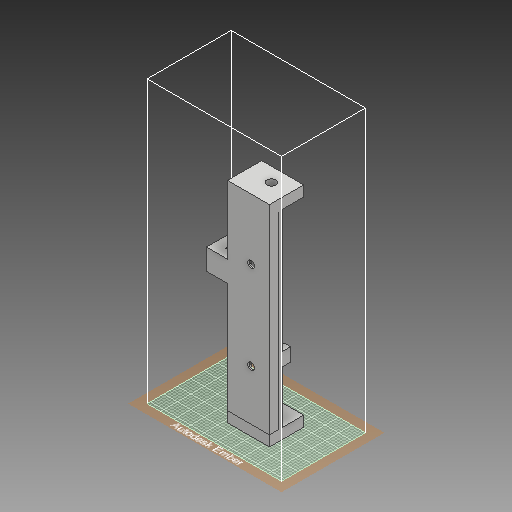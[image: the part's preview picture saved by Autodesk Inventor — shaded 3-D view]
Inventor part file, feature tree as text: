
AUTODESK INVENTOR PART (.ipt)
format: ipt  version: 2018 (Build 220112000, 112)  size: 651,776 bytes
history: native  units: mm
features: sketch x44, extrude x31, hole x8, fillet x6
ambient origin geometry x8: Origin, YZ Plane, XZ Plane, XY Plane, X Axis, Y Axis, Z Axis, Center Point
bodies: Solid1 (feature_tree)
feature tree (89):
  extrude  "Extrusion1"  Depth=100.0mm
  extrude  "Extrusion2"  Depth=5.0mm
  sketch  "Sketch3"  dims[d5=5.0mm d6=40.0mm d7=0.0mm]
  hole  "Hole1"  [1 undecoded]
  extrude  "Extrusion3"  Depth=2.0mm
  hole  "Hole2"  [1 undecoded]
  fillet  "Fillet1"  Radius=8.5mm
  extrude  "Extrusion4"  TaperAngle=90.0deg  [1 undecoded]
  extrude  "Extrusion5"  TaperAngle=180.0deg  [1 undecoded]
  hole  "Hole3"  [1 undecoded]
  fillet  "Fillet2"  Radius=3.5mm
  extrude  "Extrusion6"  Depth=10.0mm
  extrude  "Extrusion7"  Depth=5.0mm TaperAngle=0.0deg
  extrude  "Extrusion8"  Depth=5.0mm TaperAngle=0.0deg
  extrude  "Extrusion9"  Depth=0.1mm
  hole  "Hole4"  [1 undecoded]
  extrude  "Extrusion10"  Depth=5.5mm
  hole  "Hole5"  [1 undecoded]
  extrude  "Extrusion11"  Depth=2.1mm TaperAngle=0.0deg
  extrude  "Extrusion12"  Depth=5.0mm
  extrude  "Extrusion13"  Depth=1.0mm TaperAngle=0.0deg
  extrude  "Extrusion14"  Depth=3.8mm TaperAngle=0.0deg
  sketch  "Sketch21"  dims[d66=6.35mm d67=3.8mm d68=0.0mm]
  extrude  "Extrusion15"  Depth=8.0mm TaperAngle=0.0deg
  sketch  "Sketch23"  dims[d78=3.3mm d79=6.0mm d80=4.0mm d81=2.0mm d82=90.0deg d83=80.0mm d84=20.594885mm d85=5.45mm]
  extrude  "Extrusion16"  Depth=2.0mm
  extrude  "Extrusion17"  Depth=10.5mm
  hole  "Hole6"  [1 undecoded]
  fillet  "Fillet3"  Radius=4.5mm
  extrude  "Extrusion18"  Depth=8.0mm TaperAngle=0.0deg
  sketch  "Sketch28"  dims[d100=4.1mm d101=0.0mm d102=5.0mm]
  extrude  "Extrusion19"  Depth=10.0mm
  extrude  "Extrusion20"  Depth=5.0mm
  extrude  "Extrusion21"  Depth=10.0mm TaperAngle=0.0deg
  hole  "Hole7"  [1 undecoded]
  extrude  "Extrusion22"  Depth=21.0mm
  extrude  "Extrusion23"  Depth=7.499983mm TaperAngle=0.0deg
  fillet  "Fillet4"  Radius=50.0mm
  fillet  "Fillet5"  Radius=7.499983mm
  extrude  "Extrusion24"  Depth=10.0mm
  extrude  "Extrusion25"  Depth=4.1mm TaperAngle=0.0deg
  hole  "Hole8"  [1 undecoded]
  extrude  "Extrusion26"  Depth=8.0mm TaperAngle=0.0deg
  sketch  "Sketch39"  dims[d142=3.85mm d143=0.0mm d144=3.0mm]
  extrude  "Extrusion27"  Depth=1.0mm
  extrude  "Extrusion28"  Depth=3.0mm
  extrude  "Extrusion29"  Depth=100.0mm TaperAngle=0.0deg
  extrude  "Extrusion30"  Depth=10.0mm
  extrude  "Extrusion31"  Depth=7.5mm
  fillet  "Fillet6"  Radius=7.5mm
  sketch  "Sketch1"  dims[d0=22.65mm d1=100.0mm]
  sketch  "Sketch2"  dims[d2=5.0mm d3=0.0mm d4=5.0mm]
  sketch  "Sketch4"  dims[d8=10.0mm]
  sketch  "Sketch5"  dims[d9=4.0mm d10=6.0mm d11=4.0mm d12=2.0mm d13=90.0deg d14=115.0mm d15=20.594885mm d16=23.0mm]
  sketch  "Sketch6"  dims[d17=102.75mm d18=0.0mm d19=1.175mm d20=8.5mm]
  sketch  "Sketch7"  dims[d21=21.0mm d22=90.0deg]
  sketch  "Sketch8"  dims[d23=8.5mm d24=180.0deg]
  sketch  "Sketch9"  dims[d25=21.0mm]
  sketch  "Sketch10"  dims[d26=4.0mm d27=6.0mm d28=4.0mm d29=2.0mm d30=90.0deg d31=115.0mm d32=20.594885mm d33=1.0mm d34=3.5mm]
  sketch  "Sketch11"  dims[d35=15.825mm d36=10.0mm]
  sketch  "Sketch12"  dims[d37=10.0mm d38=5.0mm d39=0.0mm]
  sketch  "Sketch13"  dims[d40=5.0mm d41=12.5mm d42=0.0mm]
  sketch  "Sketch14"  dims[d43=6.0mm d44=6.0mm d45=4.0mm d46=2.0mm d47=90.0deg d48=115.0mm d49=20.594885mm d50=0.1mm]
  sketch  "Sketch15"  dims[d51=4.25mm d52=1000.0mm d53=0.0mm]
  sketch  "Sketch16"  dims[d54=3.3mm d55=5.5mm]
  sketch  "Sketch17"  dims[d56=3.2mm d57=3.0mm]
  sketch  "Sketch18"  dims[d58=2.1mm d59=91.25mm d60=0.0mm]
  sketch  "Sketch19"  dims[d61=4.44mm d62=5.0mm]
  sketch  "Sketch20"  dims[d63=1.0mm d64=91.25mm d65=0.0mm]
  sketch  "Sketch22"  dims[d69=3.3mm d70=6.0mm d71=4.0mm d72=2.0mm d73=90.0deg d74=8.0mm d75=20.594885mm d76=4.55mm d77=0.0mm]
  sketch  "Sketch24"  dims[d86=129.8mm d87=0.0mm d88=10.5mm]
  sketch  "Sketch25"  dims[d89=2.5mm d90=0.0mm d91=10.0mm d92=4.5mm d93=0.0mm]
  sketch  "Sketch26"  dims[d94=8.0mm d95=0.0mm d96=15.5mm d97=0.0mm]
  sketch  "Sketch27"  dims[d98=10.0mm d99=10.0mm]
  sketch  "Sketch29"  dims[d103=17.5mm d104=10.0mm d105=0.0mm]
  sketch  "Sketch30"  dims[d106=5.0mm]
  sketch  "Sketch31"  dims[d107=6.0mm d108=6.0mm d109=4.0mm d110=2.0mm d111=90.0deg d112=80.0mm d113=20.594885mm d114=2.0mm]
  sketch  "Sketch32"  dims[d115=45.0mm d116=0.0mm d117=21.0mm]
  sketch  "Sketch33"  dims[d118=4.5mm d119=118.0mm d120=0.0mm d121=50.0mm d122=7.499983mm]
  sketch  "Sketch34"  dims[d123=7.5mm d124=10.0mm]
  sketch  "Sketch35"  dims[d125=10.0mm d126=4.1mm d127=0.0mm]
  sketch  "Sketch36"  dims[d128=13.4mm d129=0.0mm d130=5.0mm]
  sketch  "Sketch37"  dims[d131=6.0mm d132=6.0mm d133=4.0mm d134=2.0mm d135=90.0deg d136=8.0mm d137=20.594885mm d138=130.4mm d139=0.0mm]
  sketch  "Sketch38"  dims[d140=1.0mm d141=1.0mm]
  sketch  "Sketch40"  dims[d145=2.0mm d146=100.0mm d147=0.0mm]
  sketch  "Sketch41"  dims[d148=4.0mm d149=10.0mm]
  sketch  "Sketch42"  dims[d150=5.0mm d151=15.0mm d152=7.5mm]
  sketch  "Sketch43"  dims[d153=7.5mm d154=0.0mm]
  sketch  "Sketch44"  dims[d155=6.0mm d156=6.0mm d157=4.0mm d158=2.0mm d159=90.0deg d160=8.0mm d161=20.594885mm d162=5.5mm d163=5.0mm d164=0.0mm d165=5.5mm d166=0.0mm d167=2.0mm d168=0.0mm d169=2.0mm d170=0.0mm d171=2.0mm d172=0.0mm d173=20.0mm d174=3.3mm d175=10.0mm d176=0.0mm d177=2.0mm]
note: 10 required parameter values undecoded (feature->parameter linkage not recoverable at this tier; creation-order binding heuristic only, values carry confidence <= 0.55)
